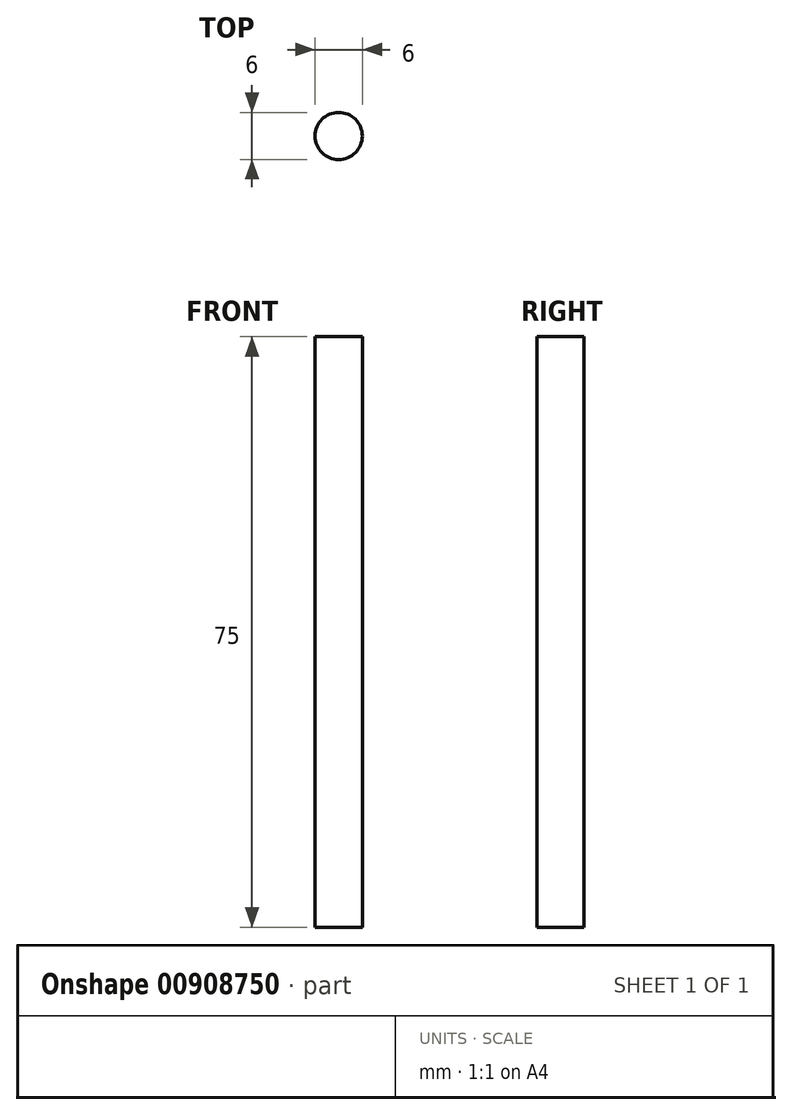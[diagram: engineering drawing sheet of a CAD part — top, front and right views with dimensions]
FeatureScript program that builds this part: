
annotation { "Feature Type Name" : "Feature", "Feature Type Description" : "" }
export const myFeature = defineFeature(function(context is Context, id is Id, definition is map)
    precondition{}
    {
        {
            var Q0;
            Q0=qCreatedBy(makeId("Top.planeOp"),FACE);
            var sketch = newSketch(context, id + "F0", { "sketchPlane" : qUnion([Q0])});
            skCircle(sketch, "E0", {"center": v(-10.8, 8.8) * mm, "radius": 3 * mm});
            skSolve(sketch);
        }
        {
            var Q0;
            Q0 = qSketchRegion(id + "F0", true);
            extrude(context, id + "F1", {"entities" : qUnion([Q0]), "depth" : 75 * mm, "offsetDistance" : 25 * mm});
        }
    });
